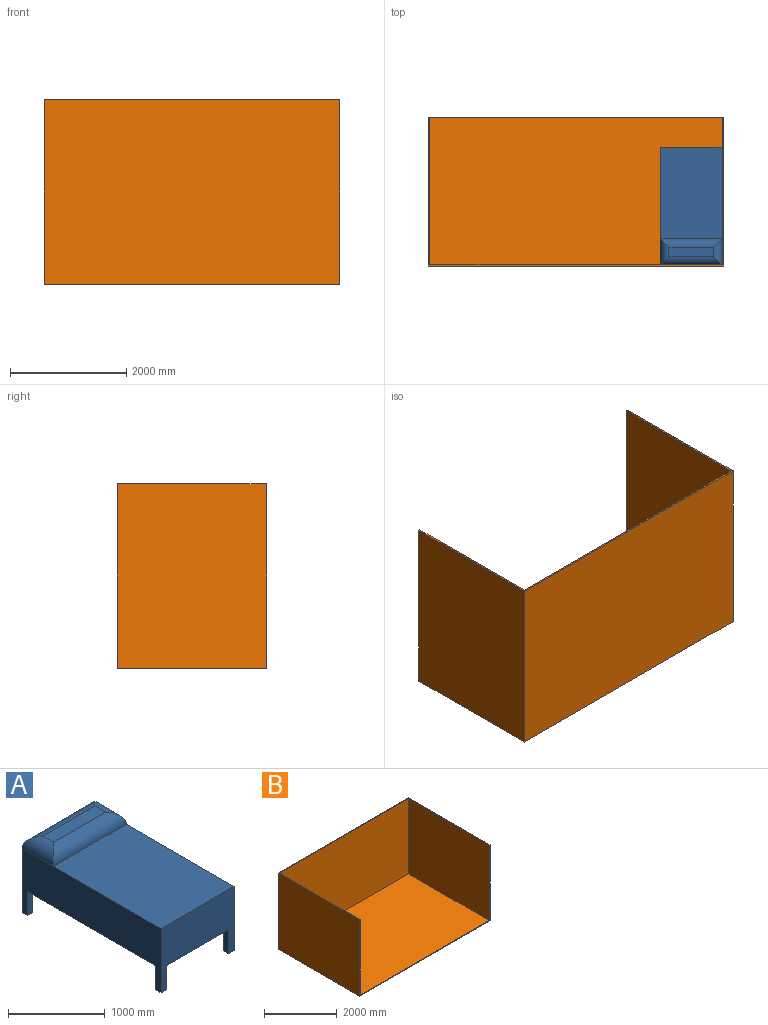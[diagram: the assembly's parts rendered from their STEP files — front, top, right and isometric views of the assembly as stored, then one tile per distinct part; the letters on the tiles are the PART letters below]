
ASSEMBLY  parts=2 mates=1
PART A: 23 faces, bbox 1066.8x2032x965.2 mm
  f0: plane 1066.8x812.8mm, normal (0,1,0), area 588385.9mm2, adj f1,f3,f4,f5,f6,f8,f9,f20
  f1: plane 2032x812.8mm, normal (-1,0,0), area 1078707.5mm2, adj f0,f2,f4,f5,f10,f11,f13,f17
  f2: plane 304.8x76.2mm, normal (0,-1,0), area 23225.8mm2, adj f1,f3,f4,f5
  f3: plane 304.8x76.2mm, normal (1,0,0), area 23225.8mm2, adj f0,f2,f4,f5
  f4: plane 76.2x76.2mm, normal (0,0,-1), area 5806.4mm2, adj f0,f1,f2,f3
  f5: plane 2032x1066.8mm, normal (0,0,-1), area 2144511.8mm2, adj f0,f1,f2,f3,f6,f7,f8,f10
  f6: plane 304.8x76.2mm, normal (-1,0,0), area 23225.8mm2, adj f0,f5,f7,f9
  f7: plane 304.8x76.2mm, normal (0,-1,0), area 23225.8mm2, adj f5,f6,f8,f9
  f8: plane 2032x812.8mm, normal (1,0,0), area 1078707.5mm2, adj f0,f5,f7,f9,f11,f14,f16,f17
  f9: plane 76.2x76.2mm, normal (0,0,-1), area 5806.4mm2, adj f0,f6,f7,f8
  f10: plane 304.8x76.2mm, normal (0,1,0), area 23225.8mm2, adj f1,f5,f12,f13
  f11: plane 1066.8x812.8mm, normal (0,-1,0), area 588385.9mm2, adj f1,f5,f8,f12,f13,f15,f16,f17
  f12: plane 304.8x76.2mm, normal (1,0,0), area 23225.8mm2, adj f5,f10,f11,f13
  f13: plane 76.2x76.2mm, normal (0,0,-1), area 5806.4mm2, adj f1,f10,f11,f12
  f14: plane 304.8x76.2mm, normal (0,1,0), area 23225.8mm2, adj f5,f8,f15,f16
  f15: plane 304.8x76.2mm, normal (-1,0,0), area 23225.8mm2, adj f5,f11,f14,f16
  f16: plane 76.2x76.2mm, normal (0,0,-1), area 5806.4mm2, adj f8,f11,f14,f15
  f17: plane 1574.8x1066.8mm, normal (0,0,1), area 1679996.6mm2, adj f1,f8,f11,f21
  f18: plane 762x152.4mm, normal (0,0,1), area 116128.8mm2, adj f19,f20,f21,f22
  f19: cylinder r=152.4mm len=457.2mm, axis (0,1,0), area 82934.5mm2, adj f1,f18,f20,f21
  f20: cylinder r=152.4mm len=1066.8mm, axis (1,0,0), area 228866.2mm2, adj f0,f18,f19,f22
  f21: cylinder r=152.4mm len=1066.8mm, axis (-1,0,0), area 228866.2mm2, adj f17,f18,f19,f22
  f22: cylinder r=152.4mm len=457.2mm, axis (0,-1,0), area 82934.5mm2, adj f8,f18,f20,f21
PART B: 13 faces, bbox 5080x3175.1x2565.4 mm
  f0: plane 3175x2565.4mm, normal (1,0,0), area 8145145mm2, adj f1,f3,f5,f9,f11
  f1: plane 5080x2565.4mm, normal (0,1,0), area 13032232mm2, adj f0,f2,f5,f11
  f2: plane 3175x2565.4mm, normal (-1,0,0), area 8145145mm2, adj f1,f3,f5,f10,f11
  f3: plane 5080x25.4mm, normal (0,-1,0), area 129032mm2, adj f0,f2,f4,f5,f12
  f4: plane 5054.6x3149.6mm, normal (0,0,1), area 15839969.3mm2, adj f3,f6,f7,f8,f9
  f5: plane 5080x3175mm, normal (0,0,-1), area 16129000mm2, adj f0,f1,f2,f3
  f6: plane 3149.67x2540mm, normal (1,0,0), area 8000165.8mm2, adj f4,f7,f10,f11,f12
  f7: plane 5029.2x2540mm, normal (0,-1,0), area 12774168mm2, adj f4,f6,f8,f11
  f8: plane 3149.53x2540mm, normal (-1,0,0), area 7999795.7mm2, adj f4,f7,f9,f11
  f9: plane 2540x25.4mm, normal (0,-1,0), area 64516.3mm2, adj f0,f4,f8,f11
  f10: plane 2540x25.4mm, normal (0,-1,0), area 64516.3mm2, adj f2,f6,f11,f12
  f11: plane 5080x3175.07mm, normal (0,0,1), area 289031.6mm2, adj f0,f1,f2,f6,f7,f8,f9,f10
  f12: plane 25.4x0.07mm, normal (0,0,-1), area 0.9mm2, adj f3,f6,f10
PLACE A rot(axis=(0,0,-1),180deg) t=(1981.2,-254,0)mm
PLACE B rot(axis=(-1,0,0),90deg) t=(0,-1295.4,1562.1)mm
MATE fastened B.f7 <-> A.f4  axis (0,0,1) through (2514.6,-1270,0)mm
